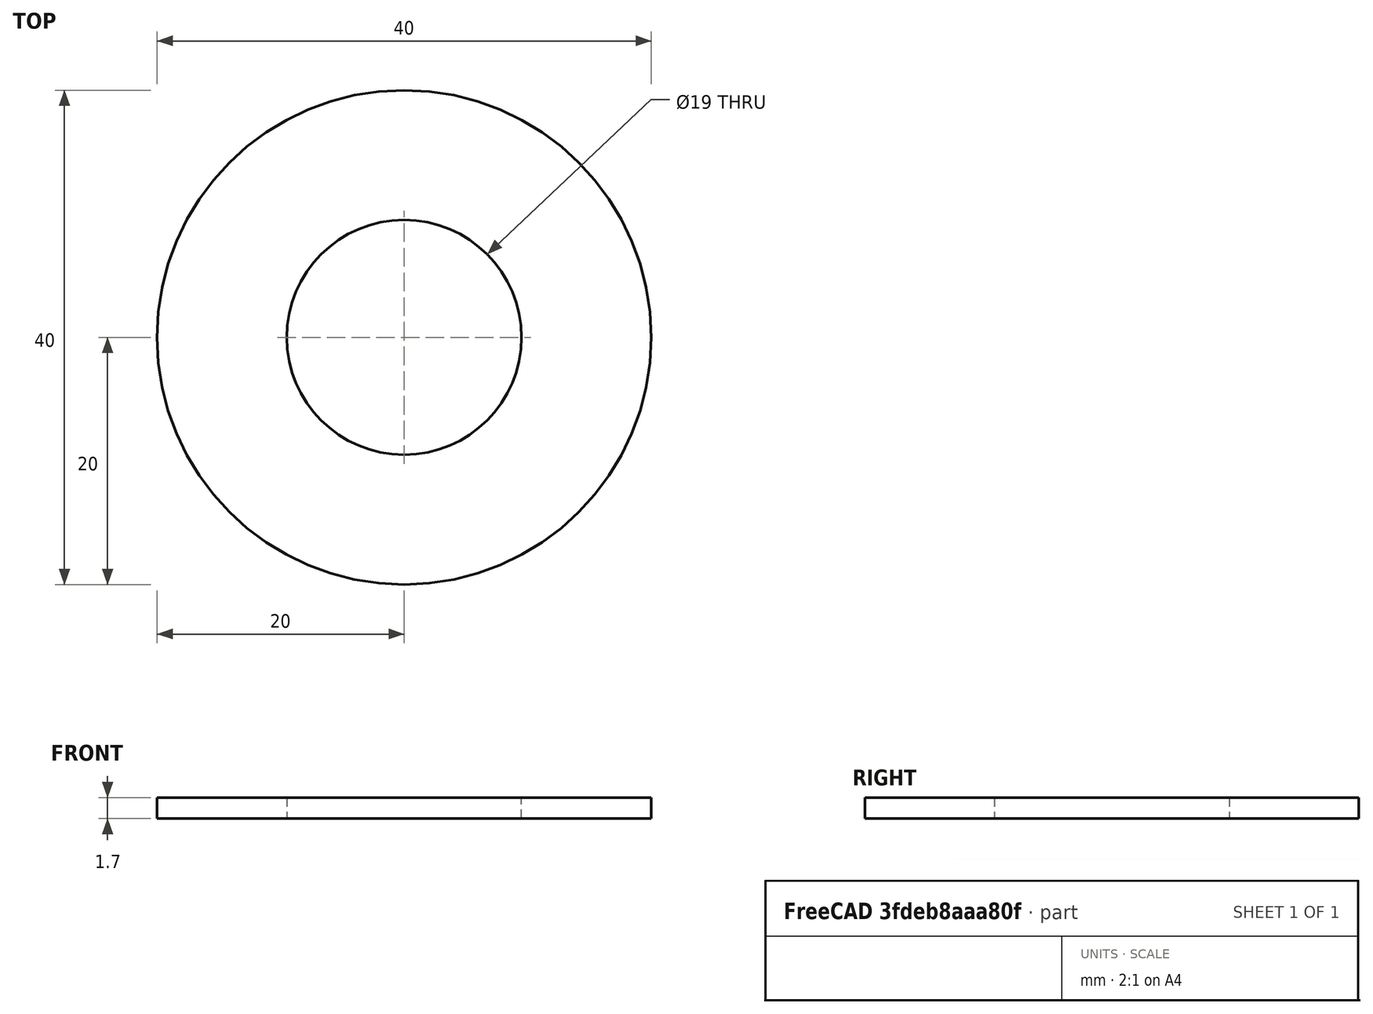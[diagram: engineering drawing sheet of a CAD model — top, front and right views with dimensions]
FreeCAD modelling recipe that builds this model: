
FCSTD DOCUMENT  (FreeCAD 0.20R29603 (Git))
Label: maska_tipke_za_farbanje_2x
License: All rights reserved
LicenseURL: http://en.wikipedia.org/wiki/All_rights_reserved
objects: Sketcher::SketchObject×1, PartDesign::Pad×1, PartDesign::Body×1
note: 4 computed .brp shape members not serialized (recipe doc carries the construction recipe); baked Part::Feature solids carry a one-line shape summary decoded from their .brp

FEATURE [Sketcher::SketchObject] Sketch
  FullyConstrained = true
  MapMode = 5
  Support = -> [XY_Plane]
  sketch-geometry (2):
    g0: Circle CenterX=0 CenterY=0 CenterZ=0 NormalX=0 NormalY=0 NormalZ=1 AngleXU=0 Radius=9.5
    g1: Circle CenterX=0 CenterY=0 CenterZ=0 NormalX=0 NormalY=0 NormalZ=1 AngleXU=0 Radius=20
  constraints (4):
    c: Coincident(g0,g-1)
    c: Coincident(g1,g0)
    c: Diameter(g0) = 19
    c: Diameter(g1) = 40
FEATURE [PartDesign::Pad] Pad
  Direction = (0,0,1)
  Length = 1.7
  Length2 = 10
  Profile = -> Sketch
  ReferenceAxis = -> Sketch [N_Axis]
  Type = 0
FEATURE [PartDesign::Body] Body
  Group = -> [Sketch,Pad]
  Origin = -> Origin
  Tip = -> Pad
